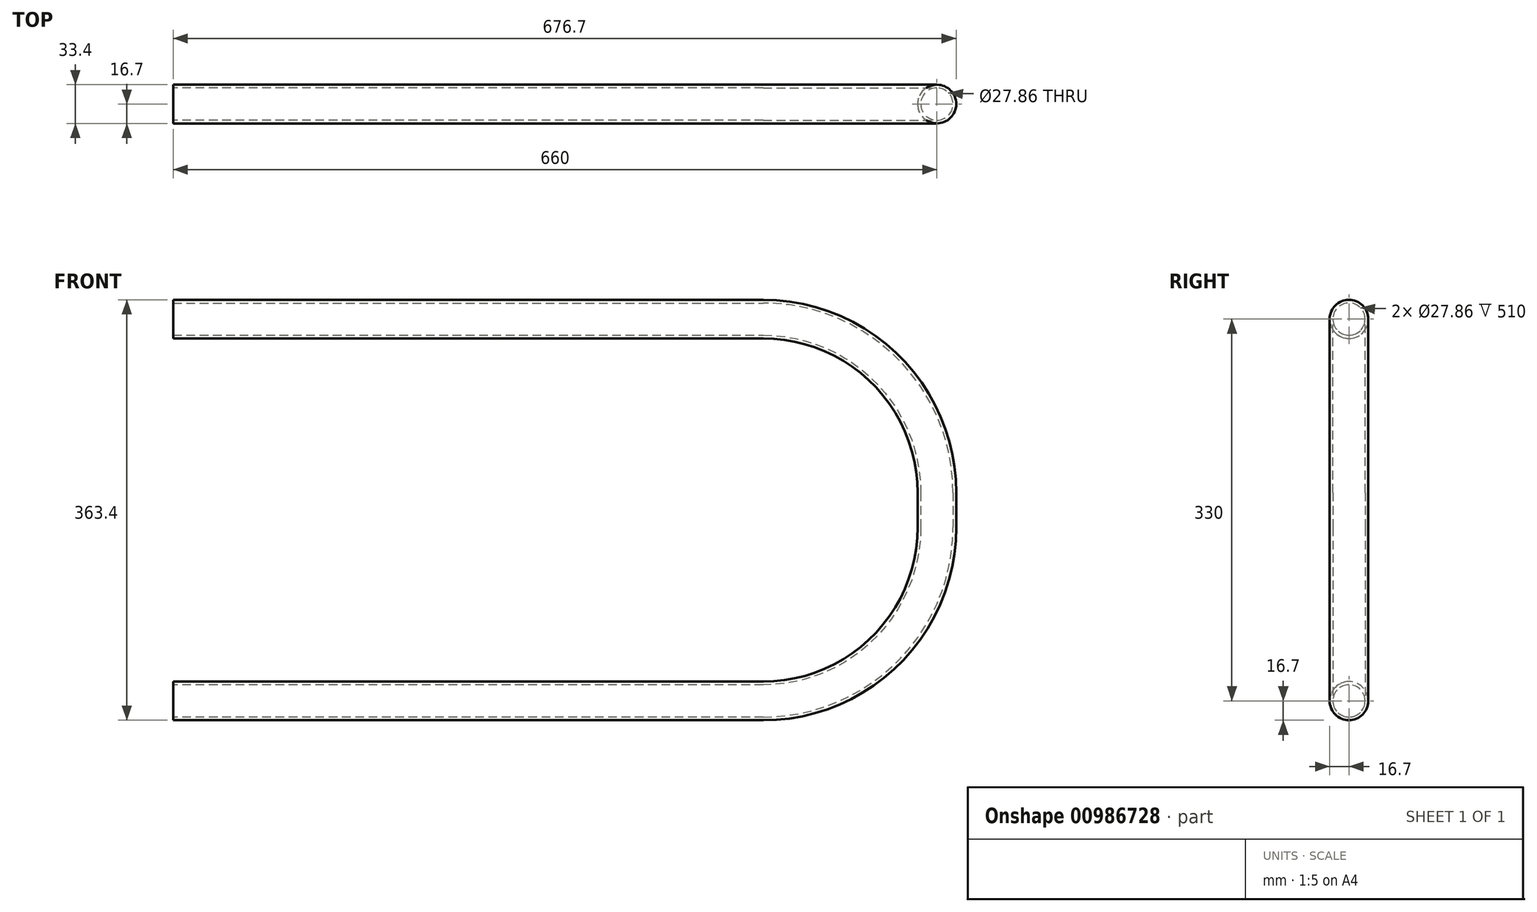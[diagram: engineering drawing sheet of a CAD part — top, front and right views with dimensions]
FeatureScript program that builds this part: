
annotation { "Feature Type Name" : "Feature", "Feature Type Description" : "" }
export const myFeature = defineFeature(function(context is Context, id is Id, definition is map)
    precondition{}
    {
        {
            var Q0;
            Q0=qCreatedBy(makeId("Front.planeOp"),FACE);
            var sketch = newSketch(context, id + "F0", { "sketchPlane" : qUnion([Q0])});
            skLineSegment(sketch, "E0", {"start": v(0, 0) * mm, "end": v(510, 0) * mm});
            skLineSegment(sketch, "E1", {"start": v(660, -150) * mm, "end": v(660, -180) * mm});
            skLineSegment(sketch, "E2", {"start": v(510, -330) * mm, "end": v(0, -330) * mm});
            skPoint(sketch, "E3.visualSharp", {"position": v(660, 0) * mm});
            skArc(sketch, "E3.filletArc", {"start": v(660, -150) * mm, "mid": v(616.07, -43.93) * mm, "end": v(510, 0) * mm});
            skPoint(sketch, "E4.visualSharp", {"position": v(660, -330) * mm});
            skArc(sketch, "E4.filletArc", {"start": v(510, -330) * mm, "mid": v(616.07, -286.07) * mm, "end": v(660, -180) * mm});
            skSolve(sketch);
        }
        {
            var Q0;
            Q0=qCreatedBy(makeId("Right.planeOp"),FACE);
            var sketch = newSketch(context, id + "F1", { "sketchPlane" : qUnion([Q0])});
            skCircle(sketch, "E5", {"center": v(0, 0) * mm, "radius": 16.7 * mm});
            skCircle(sketch, "E6.0", {"center": v(0, 0) * mm, "radius": 13.93 * mm});
            skSolve(sketch);
        }
        {
            var Q0;
            Q0=makeQuery(id+"F1.imprint","IMPRINT",FACE,{"disambiguationData":[TD([[makeQuery(id+"F1.imprint","IMPRINT",EDGE,{"derivedFrom":sQuery(id+"F1.wireOp",EDGE,"E5")}),1.0]])]});
            var Q1;
            Q1=sQuery(id+"F0.wireOp",EDGE,"E0");
            var Q2;
            Q2=sQuery(id+"F0.wireOp",EDGE,"E3.filletArc");
            var Q3;
            Q3=sQuery(id+"F0.wireOp",EDGE,"E1");
            var Q4;
            Q4=sQuery(id+"F0.wireOp",EDGE,"E4.filletArc");
            var Q5;
            Q5=sQuery(id+"F0.wireOp",EDGE,"E2");
            sweep(context, id + "F2", {"profiles" : qUnion([Q0]), "path" : qUnion([Q1, Q2, Q3, Q4, Q5])});
        }
    });
